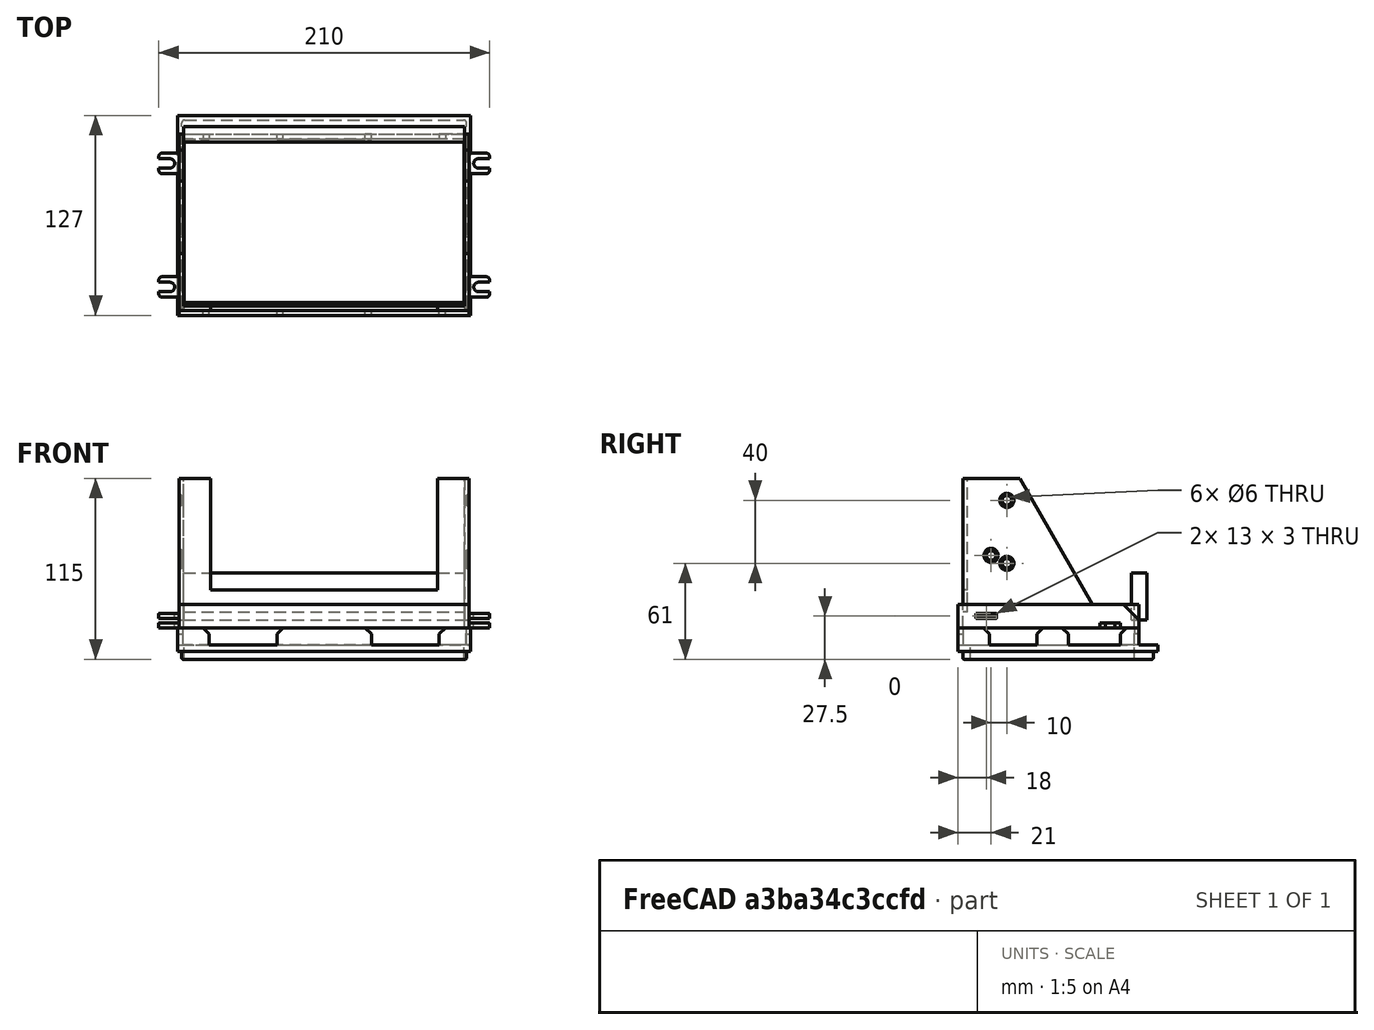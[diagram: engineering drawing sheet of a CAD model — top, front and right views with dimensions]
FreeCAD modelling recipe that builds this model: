
FCSTD DOCUMENT  (FreeCAD 0.15R4671 (Git))
Label: mount
License: All rights reserved
LicenseURL: http://en.wikipedia.org/wiki/All_rights_reserved
objects: Part::Box×30, Drawing::FeatureView×27, Part::Cut×14, Part::MultiFuse×13, Part::Cylinder×7, Drawing::FeatureViewPart×6, PartDesign::Fillet×4, Part::Fuse×2, Part::Fillet×2, Part::Chamfer×2, PartDesign::Chamfer×1, App::DocumentObjectGroup×1, Drawing::FeaturePage×1
note: 75 computed .brp shape members not serialized (recipe doc carries the construction recipe); baked Part::Feature solids carry a one-line shape summary decoded from their .brp

FEATURE [Part::Box] Box  label="Cube"
  Height = 15
  Length = 184
  Placement = pos=(1,0,5) rot=(0,0,1;0rad)
  Width = 115
FEATURE [Part::Box] Box001  label="Cube001"
  Height = 30
  Length = 178.5
  Placement = pos=(3.75,3,10) rot=(0,0,1;0rad)
  Width = 109
FEATURE [Part::Cylinder] Cylinder
  Angle = 360
  Height = 10
  Placement = pos=(7,6.5,0) rot=(0,0,1;0rad)
  Radius = 3
FEATURE [Part::Box] Box003  label="Cube003"
  Height = 10
  Length = 7
  Placement = pos=(0,3.5,0) rot=(0,0,1;0rad)
  Width = 6
FEATURE [PartDesign::Fillet] Fillet001
  Radius = 2
FEATURE [Part::MultiFuse] Fusion
  Shapes = -> [Box003,Cylinder]
FEATURE [Part::Cut] Cut001  label="Mounting Point 001"
  Base = -> Fillet001
  Placement = pos=(-12,11.5,11) rot=(0,0,1;0rad)
  Tool = -> Fusion
FEATURE [Part::Cylinder] Cylinder001
  Angle = 360
  Height = 10
  Placement = pos=(7,6.5,0) rot=(0,0,1;0rad)
  Radius = 3
FEATURE [Part::Box] Box005  label="Cube005"
  Height = 10
  Length = 7
  Placement = pos=(0,3.5,0) rot=(0,0,1;0rad)
  Width = 6
FEATURE [PartDesign::Fillet] Fillet003
  Radius = 2
FEATURE [Part::MultiFuse] Fusion001
  Shapes = -> [Box005,Cylinder001]
FEATURE [Part::Cut] Cut002  label="Mounting Point 002"
  Base = -> Fillet003
  Placement = pos=(-12,90,5) rot=(0,0,1;0rad)
  Tool = -> Fusion001
FEATURE [Part::Cylinder] Cylinder002
  Angle = 360
  Height = 10
  Placement = pos=(7,6.5,0) rot=(0,0,1;0rad)
  Radius = 3
FEATURE [Part::Box] Box007  label="Cube007"
  Height = 10
  Length = 7
  Placement = pos=(0,3.5,0) rot=(0,0,1;0rad)
  Width = 6
FEATURE [PartDesign::Fillet] Fillet005
  Radius = 2
FEATURE [Part::MultiFuse] Fusion002
  Shapes = -> [Box007,Cylinder002]
FEATURE [Part::Cut] Cut003  label="Mounting Point 003"
  Base = -> Fillet005
  Placement = pos=(198,24.5,11) rot=(0,0,1;3.14159rad)
  Tool = -> Fusion002
FEATURE [Part::Cylinder] Cylinder003
  Angle = 360
  Height = 10
  Placement = pos=(7,6.5,0) rot=(0,0,1;0rad)
  Radius = 3
FEATURE [Part::Box] Box009  label="Cube009"
  Height = 10
  Length = 7
  Placement = pos=(0,3.5,0) rot=(0,0,1;0rad)
  Width = 6
FEATURE [PartDesign::Fillet] Fillet007
  Radius = 2
FEATURE [Part::MultiFuse] Fusion003
  Shapes = -> [Box009,Cylinder003]
FEATURE [Part::Cut] Cut004  label="Mounting Point 004"
  Base = -> Fillet007
  Placement = pos=(198,103,5) rot=(0,0,1;3.14159rad)
  Tool = -> Fusion003
FEATURE [Part::Box] Box010  label="Cube010"
  Height = 80
  Length = 2.75
  Placement = pos=(0,10,30) rot=(0,0,1;0rad)
  Width = 80
FEATURE [Part::Box] Box011  label="Cube011"
  Height = 80
  Length = 4
  Placement = pos=(0,38,119) rot=(-1,0,0;1.0472rad)
  Width = 150
FEATURE [Part::Cut] Cut005
  Base = -> Box010
  Tool = -> Box011
FEATURE [Part::Box] Box012  label="Cube012"
  Height = 80
  Length = 20
  Placement = pos=(0,7,30) rot=(0,0,1;0rad)
  Width = 3
FEATURE [Part::Fuse] Fusion005  label="Left Support"
  Base = -> Cut005
  Placement = pos=(0,-3,0) rot=(0,0,1;0rad)
  Tool = -> Box012
FEATURE [Part::Box] Box013  label="Cube013"
  Height = 80
  Length = 2.75
  Placement = pos=(-2.75,10,30) rot=(0,0,1;0rad)
  Width = 80
FEATURE [Part::Box] Box014  label="Cube014"
  Height = 80
  Length = 4
  Placement = pos=(-2.75,38,119) rot=(-1,0,0;1.0472rad)
  Width = 150
FEATURE [Part::Cut] Cut006
  Base = -> Box013
  Tool = -> Box014
FEATURE [Part::Box] Box015  label="Cube015"
  Height = 80
  Length = 20
  Placement = pos=(-20,7,30) rot=(0,0,1;0rad)
  Width = 3
FEATURE [Part::Fuse] Fusion006  label="Right Support"
  Base = -> Cut006
  Placement = pos=(184,-3,0) rot=(0,0,1;0rad)
  Tool = -> Box015
FEATURE [Part::Box] Box016  label="Cross Brace"
  Height = 14
  Length = 184
  Placement = pos=(0,4,25) rot=(0,0,1;0rad)
  Width = 3
FEATURE [Part::Box] Box017  label="Lip"
  Height = 4
  Length = 186
  Width = 127
FEATURE [Part::Box] Box018  label="Cutout"
  Height = 30
  Length = 178
  Placement = pos=(4,8,-25) rot=(0,0,1;0rad)
  Width = 104
FEATURE [Part::Box] Box019  label="Cube016"
  Height = 5
  Length = 181
  Placement = pos=(2.5,3,-5) rot=(0,0,1;0rad)
  Width = 121
FEATURE [Part::MultiFuse] Fusion007
  Shapes = -> [Box017,Box019]
FEATURE [Part::Cut] Cut007
  Base = -> Fusion007
  Tool = -> Box018
FEATURE [Part::Fillet] Fillet008  label="Fill Plate"
  Base = -> Cut007
  Edges = 4 edges r=2: [Edge30,Edge31,Edge32,Edge35]
FEATURE [Part::MultiFuse] Fusion008  label="Carrier"
  Placement = pos=(1,-1,0) rot=(0,0,1;0rad)
  Shapes = -> [Fusion005,Fusion006,Box016]
FEATURE [Part::MultiFuse] Fusion009
  Placement = pos=(0,0,10) rot=(0,0,1;0rad)
  Shapes = -> [Box,Cut001,Cut002,Cut003,Cut004]
FEATURE [Part::Cut] Cut  label="Mount Points"
  Base = -> Fusion009
  Tool = -> Box001
FEATURE [Part::Box] Box020  label="Cube017"
  Height = 30
  Length = 178.5
  Placement = pos=(3.75,110,20) rot=(0,0,1;0rad)
  Width = 10
FEATURE [PartDesign::Chamfer] Chamfer  label="Carrier Frame"
  Size = 10
FEATURE [Part::Box] Box021  label="Cube018"
  Height = 11
  Length = 20
  Width = 20
FEATURE [Part::Box] Box022  label="Cube019"
  Height = 11
  Length = 30
  Placement = pos=(3,3,0) rot=(0,0,1;0rad)
  Width = 20
FEATURE [Part::Cut] Cut009
  Base = -> Box021
  Placement = pos=(0,0,4) rot=(0,0,1;0rad)
  Tool = -> Box022
FEATURE [Part::Box] Box023  label="Cube020"
  Height = 11
  Length = 20
  Width = 20
FEATURE [Part::Box] Box024  label="Cube021"
  Height = 11
  Length = 30
  Placement = pos=(3,3,0) rot=(0,0,1;0rad)
  Width = 20
FEATURE [Part::Cut] Cut010
  Base = -> Box023
  Placement = pos=(186,0,15) rot=(0,1,0;3.14159rad)
  Tool = -> Box024
FEATURE [Part::Box] Box025  label="Cube022"
  Height = 11
  Length = 3
  Placement = pos=(0,50,4) rot=(0,0,1;0rad)
  Width = 20
FEATURE [Part::Box] Box026  label="Cube023"
  Height = 11
  Length = 3
  Placement = pos=(183,50,4) rot=(0,0,1;0rad)
  Width = 20
FEATURE [Part::MultiFuse] Fusion012  label="Carrier (No Mounts)"
  Shapes = -> [Chamfer,Fusion008]
FEATURE [Drawing::FeatureViewPart] Ortho  label="Ortho_0_0"
  Direction = (0,0,-1)
  HiddenWidth = 0.15
  LineWidth = 0.35
  Rotation = 180
  ShowHiddenLines = false
  ShowSmoothLines = false
  Source = -> Fusion012
  Tolerance = 0.05
  ViewResult = <blob: 2978 chars omitted>
  Visible = true
  X = 60
  Y = 220
FEATURE [Drawing::FeatureView] dim007
  Rotation = 0
  ViewResult = <g> \n  <line x1="48.000000" y1="231.500000" x2="48.000000" y2="209.663479" style="stroke:rgb(0,0,0);stroke-width:0.30" />\n<line x1="61.000000" y1="218.000000" x2="61.000000" y2="209.663479" style="stroke:rgb(0,0,0);stroke-width:0.30" />\n<line x1="48.000000" y1="210.663479" x2="61.000000" y2="210.663479" style="stroke:rgb(0,0,0);stroke-width:0.30" /> \n  <polygon points="61.000000,210.663479 58.000000,209.663479 57.000000,210.663479 58.000000,211.663479" style="fill:rgb(0,0,0);stroke:rgb(0,0,0);stroke-width:0" /><polygon points="48.000000,210.663479 51.000000,211.663479 52.000000,210.663479 51.000000,209.663479" style="fill:rgb(0,0,0);stroke:rgb(0,0,0);stroke-width:0" /> \n  <text x="54.500000" y="208.663479" font-family="arial" font-size="3.6" fill="rgb(0,0,0)" text-anchor="middle" transform="rotate(0.000000 54.500000,208.663479)" >13</text> </g>
  Visible = true
  X = 0
  Y = 0
FEATURE [Drawing::FeatureView] dim008
  Rotation = 0
  ViewResult = <g> \n  <line x1="48.000000" y1="231.500000" x2="34.256570" y2="231.500000" style="stroke:rgb(0,0,0);stroke-width:0.30" />\n<line x1="48.000000" y1="244.500000" x2="34.256570" y2="244.500000" style="stroke:rgb(0,0,0);stroke-width:0.30" />\n<line x1="35.256570" y1="231.500000" x2="35.256570" y2="244.500000" style="stroke:rgb(0,0,0);stroke-width:0.30" /> \n  <polygon points="35.256570,244.500000 36.256570,241.500000 35.256570,240.500000 34.256570,241.500000" style="fill:rgb(0,0,0);stroke:rgb(0,0,0);stroke-width:0" /><polygon points="35.256570,231.500000 34.256570,234.500000 35.256570,235.500000 36.256570,234.500000" style="fill:rgb(0,0,0);stroke:rgb(0,0,0);stroke-width:0" /> \n  <text x="33.256570" y="238.000000" font-family="arial" font-size="3.6" fill="rgb(0,0,0)" text-anchor="middle" transform="rotate(-90.000000 33.256570,238.000000)" >13</text> </g>
  Visible = true
  X = 0
  Y = 0
FEATURE [Drawing::FeatureView] dim009
  Rotation = 0
  ViewResult = <g> \n  <line x1="63.750000" y1="228.000000" x2="63.750000" y2="300.005281" style="stroke:rgb(0,0,0);stroke-width:0.30" />\n<line x1="242.250000" y1="228.000000" x2="242.250000" y2="300.005281" style="stroke:rgb(0,0,0);stroke-width:0.30" />\n<line x1="63.750000" y1="299.005281" x2="242.250000" y2="299.005281" style="stroke:rgb(0,0,0);stroke-width:0.30" /> \n  <polygon points="242.250000,299.005281 239.250000,298.005281 238.250000,299.005281 239.250000,300.005281" style="fill:rgb(0,0,0);stroke:rgb(0,0,0);stroke-width:0" /><polygon points="63.750000,299.005281 66.750000,300.005281 67.750000,299.005281 66.750000,298.005281" style="fill:rgb(0,0,0);stroke:rgb(0,0,0);stroke-width:0" /> \n  <text x="153.000000" y="297.005281" font-family="arial" font-size="3.6" fill="rgb(0,0,0)" text-anchor="middle" transform="rotate(0.000000 153.000000,297.005281)" >178.5</text> </g>
  Visible = true
  X = 0
  Y = 0
FEATURE [Drawing::FeatureView] dimStack001
  Rotation = 0
  ViewResult = <g> <line x1="244.250001" y1="226.000000" x2="267.334281" y2="226.000000" style="stroke:rgb(0,0,0);stroke-width:0.30" />\n<line x1="244.250001" y1="332.000000" x2="267.334281" y2="332.000000" style="stroke:rgb(0,0,0);stroke-width:0.30" />\n<line x1="266.334281" y1="226.000000" x2="266.334281" y2="332.000000" style="stroke:rgb(0,0,0);stroke-width:0.30" />\n<polygon points="266.334281,226.000000 265.334281,229.000000 266.334281,230.000000 267.334281,229.000000" style="fill:rgb(0,0,0);stroke:rgb(0,0,0);stroke-width:0" />\n<polygon points="266.334281,332.000000 267.334281,329.000000 266.334281,328.000000 265.334281,329.000000" style="fill:rgb(0,0,0);stroke:rgb(0,0,0);stroke-width:0" />\n<text x="264.334281" y="279.000000" font-family="arial" font-size="3.6" fill="rgb(0,0,0)" text-anchor="middle" transform="rotate(-90.000000 264.334281,279.000000)" >106</text> </g> \n<g> <line x1="244.250001" y1="226.000000" x2="274.334281" y2="226.000000" style="stroke:rgb(0,0,0);stroke-width:0.30" />\n<line x1="244.250001" y1="223.000000" x2="274.334281" y2="223.000000" style="stroke:rgb(0,0,0);stroke-width:0.30" />\n<line x1="273.334281" y1="226.000000" x2="273.334281" y2="223.000000" style="stroke:rgb(0,0,0);stroke-width:0.30" />\n<polygon points="273.334281,226.000000 272.334281,229.000000 273.334281,230.000000 274.334281,229.000000" style="fill:rgb(0,0,0);stroke:rgb(0,0,0);stroke-width:0" />\n<polygon points="273.334281,223.000000 274.334281,220.000000 273.334281,219.000000 272.334281,220.000000" style="fill:rgb(0,0,0);stroke:rgb(0,0,0);stroke-width:0" />\n<text x="271.334281" y="224.500000" font-family="arial" font-size="3.6" fill="rgb(0,0,0)" text-anchor="middle" transform="rotate(-90.000000 271.334281,224.500000)" >3</text> </g> 
  Visible = true
  X = 0
  Y = 0
FEATURE [Drawing::FeatureView] dim010
  Rotation = 0
  ViewResult = <g> \n  <line x1="61.000000" y1="337.000000" x2="61.000000" y2="354.805423" style="stroke:rgb(0,0,0);stroke-width:0.30" />\n<line x1="245.000000" y1="337.000000" x2="245.000000" y2="354.805423" style="stroke:rgb(0,0,0);stroke-width:0.30" />\n<line x1="61.000000" y1="353.805423" x2="245.000000" y2="353.805423" style="stroke:rgb(0,0,0);stroke-width:0.30" /> \n  <polygon points="245.000000,353.805423 242.000000,352.805423 241.000000,353.805423 242.000000,354.805423" style="fill:rgb(0,0,0);stroke:rgb(0,0,0);stroke-width:0" /><polygon points="61.000000,353.805423 64.000000,354.805423 65.000000,353.805423 64.000000,352.805423" style="fill:rgb(0,0,0);stroke:rgb(0,0,0);stroke-width:0" /> \n  <text x="153.000000" y="351.805423" font-family="arial" font-size="3.6" fill="rgb(0,0,0)" text-anchor="middle" transform="rotate(0.000000 153.000000,351.805423)" >184</text> </g>
  Visible = true
  X = 0
  Y = 0
FEATURE [Drawing::FeatureView] dim011
  Rotation = 0
  ViewResult = <g> \n  <line x1="313.000000" y1="220.000000" x2="298.480968" y2="220.000000" style="stroke:rgb(0,0,0);stroke-width:0.30" />\n<line x1="313.000000" y1="335.000000" x2="298.480968" y2="335.000000" style="stroke:rgb(0,0,0);stroke-width:0.30" />\n<line x1="299.480968" y1="220.000000" x2="299.480968" y2="335.000000" style="stroke:rgb(0,0,0);stroke-width:0.30" /> \n  <polygon points="299.480968,335.000000 300.480968,332.000000 299.480968,331.000000 298.480968,332.000000" style="fill:rgb(0,0,0);stroke:rgb(0,0,0);stroke-width:0" /><polygon points="299.480968,220.000000 298.480968,223.000000 299.480968,224.000000 300.480968,223.000000" style="fill:rgb(0,0,0);stroke:rgb(0,0,0);stroke-width:0" /> \n  <text x="297.480968" y="277.500000" font-family="arial" font-size="3.6" fill="rgb(0,0,0)" text-anchor="middle" transform="rotate(-90.000000 297.480968,277.500000)" >115</text> </g>
  Visible = true
  X = 0
  Y = 0
FEATURE [Drawing::FeatureView] dim012
  Rotation = 0
  ViewResult = <g> \n  <line x1="330.000000" y1="221.000000" x2="330.000000" y2="208.868834" style="stroke:rgb(0,0,0);stroke-width:0.30" />\n<line x1="410.000000" y1="221.000000" x2="410.000000" y2="208.868834" style="stroke:rgb(0,0,0);stroke-width:0.30" />\n<line x1="330.000000" y1="209.868834" x2="410.000000" y2="209.868834" style="stroke:rgb(0,0,0);stroke-width:0.30" /> \n  <polygon points="410.000000,209.868834 407.000000,208.868834 406.000000,209.868834 407.000000,210.868834" style="fill:rgb(0,0,0);stroke:rgb(0,0,0);stroke-width:0" /><polygon points="330.000000,209.868834 333.000000,210.868834 334.000000,209.868834 333.000000,208.868834" style="fill:rgb(0,0,0);stroke:rgb(0,0,0);stroke-width:0" /> \n  <text x="370.000000" y="207.868834" font-family="arial" font-size="3.6" fill="rgb(0,0,0)" text-anchor="middle" transform="rotate(0.000000 370.000000,207.868834)" >80</text> </g>
  Visible = true
  X = 0
  Y = 0
FEATURE [Drawing::FeatureView] dim013
  Rotation = 0
  ViewResult = <g> \n  <line x1="321.000000" y1="229.512600" x2="321.000000" y2="200.380915" style="stroke:rgb(0,0,0);stroke-width:0.30" />\n<line x1="315.000000" y1="218.000000" x2="315.000000" y2="200.380915" style="stroke:rgb(0,0,0);stroke-width:0.30" />\n<line x1="321.000000" y1="201.380915" x2="315.000000" y2="201.380915" style="stroke:rgb(0,0,0);stroke-width:0.30" /> \n  <polygon points="315.000000,201.380915 312.000000,200.380915 311.000000,201.380915 312.000000,202.380915" style="fill:rgb(0,0,0);stroke:rgb(0,0,0);stroke-width:0" /><polygon points="321.000000,201.380915 324.000000,202.380915 325.000000,201.380915 324.000000,200.380915" style="fill:rgb(0,0,0);stroke:rgb(0,0,0);stroke-width:0" /> \n  <text x="318.000000" y="199.380915" font-family="arial" font-size="3.6" fill="rgb(0,0,0)" text-anchor="middle" transform="rotate(0.000000 318.000000,199.380915)" >6</text> </g>
  Visible = true
  X = 0
  Y = 0
FEATURE [Drawing::FeatureView] dim014
  Rotation = 0
  ViewResult = <g> \n  <line x1="315.000000" y1="337.000000" x2="315.000000" y2="355.145058" style="stroke:rgb(0,0,0);stroke-width:0.30" />\n<line x1="330.000000" y1="327.000000" x2="330.000000" y2="355.145058" style="stroke:rgb(0,0,0);stroke-width:0.30" />\n<line x1="315.000000" y1="354.145058" x2="330.000000" y2="354.145058" style="stroke:rgb(0,0,0);stroke-width:0.30" /> \n  <polygon points="330.000000,354.145058 327.000000,353.145058 326.000000,354.145058 327.000000,355.145058" style="fill:rgb(0,0,0);stroke:rgb(0,0,0);stroke-width:0" /><polygon points="315.000000,354.145058 318.000000,355.145058 319.000000,354.145058 318.000000,353.145058" style="fill:rgb(0,0,0);stroke:rgb(0,0,0);stroke-width:0" /> \n  <text x="322.500000" y="352.145058" font-family="arial" font-size="3.6" fill="rgb(0,0,0)" text-anchor="middle" transform="rotate(0.000000 322.500000,352.145058)" >15</text> </g>
  Visible = true
  X = 0
  Y = 0
FEATURE [Part::Cylinder] Cylinder004
  Angle = 360
  Height = 200
  Placement = pos=(0,0,0) rot=(0,1,0;1.5708rad)
  Radius = 3
FEATURE [Part::Cylinder] Cylinder005
  Angle = 360
  Height = 200
  Placement = pos=(0,0,40) rot=(0,1,0;1.5708rad)
  Radius = 3
FEATURE [Part::Cylinder] Cylinder006
  Angle = 360
  Height = 200
  Placement = pos=(0,-10,5) rot=(0,1,0;1.5708rad)
  Radius = 3
FEATURE [Part::MultiFuse] Fusion013
  Placement = pos=(-5,31,56) rot=(0,0,1;0rad)
  Shapes = -> [Cylinder004,Cylinder005,Cylinder006]
FEATURE [Part::Cut] Cut011
  Base = -> Fusion012
  Tool = -> Fusion013
FEATURE [Part::Chamfer] Chamfer005  label="Carrier (Complete)"
  Base = -> Cut011
  Edges = 6 edges r=1.5: [Edge86,Edge87,Edge88,Edge199,Edge200,Edge201]
FEATURE [Drawing::FeatureViewPart] Ortho008  label="Ortho_0_003"
  Direction = (1,0,0)
  HiddenWidth = 0.15
  LineWidth = 0.35
  Rotation = 0
  ShowHiddenLines = false
  ShowSmoothLines = false
  Source = -> Chamfer005
  Tolerance = 0.05
  ViewResult = <blob: 5883 chars omitted>
  Visible = true
  X = 300
  Y = 220
FEATURE [Drawing::FeatureViewPart] Ortho010  label="Ortho_1_002"
  Direction = (0.57735,-0.57735,-0.57735)
  HiddenWidth = 0.15
  LineWidth = 0.35
  Rotation = 180
  ShowHiddenLines = false
  ShowSmoothLines = false
  Source = -> Chamfer005
  Tolerance = 0.05
  ViewResult = <blob: 11598 chars omitted>
  Visible = true
  X = 360
  Y = 60
FEATURE [Part::Box] Box029  label="Cube026"
  Height = 11
  Length = 20
  Width = 20
FEATURE [Part::Box] Box030  label="Cube027"
  Height = 11
  Length = 30
  Placement = pos=(3,3,0) rot=(0,0,1;0rad)
  Width = 20
FEATURE [Part::Cut] Cut012
  Base = -> Box029
  Placement = pos=(0,115,15) rot=(1,0,0;3.14159rad)
  Tool = -> Box030
FEATURE [Part::Box] Box031  label="Cube028"
  Height = 11
  Length = 20
  Width = 20
FEATURE [Part::Box] Box032  label="Cube029"
  Height = 11
  Length = 30
  Placement = pos=(3,3,0) rot=(0,0,1;0rad)
  Width = 20
FEATURE [Part::Cut] Cut013
  Base = -> Box031
  Placement = pos=(186,115,4) rot=(0,0,1;3.14159rad)
  Tool = -> Box032
FEATURE [Part::MultiFuse] Fusion014
  Shapes = -> [Cut009,Box025,Box026,Cut010,Cut013,Cut012]
FEATURE [Part::Box] Box033  label="Cube030"
  Height = 11
  Length = 60
  Placement = pos=(63,112,4) rot=(0,0,1;0rad)
  Width = 3
FEATURE [Part::MultiFuse] Fusion015
  Shapes = -> [Fusion014,Box033]
FEATURE [Part::Fillet] Fillet009
  Base = -> Fillet008
  Edges = 8 edges r=1: [Edge13,Edge16,Edge18,Edge21,Edge23,Edge24,Edge26,Edge28]
FEATURE [Part::Box] Box034  label="Cube031"
  Height = 20
  Length = 200
  Placement = pos=(-10,73,-5) rot=(0,0,1;0rad)
  Width = 30
FEATURE [Part::Cut] Cut014
  Base = -> Fusion015
  Tool = -> Box034
FEATURE [Part::Box] Box035  label="Cube032"
  Height = 11
  Length = 60
  Placement = pos=(63,0,4) rot=(0,0,1;0rad)
  Width = 3
FEATURE [Part::MultiFuse] Fusion016
  Shapes = -> [Cut014,Box035]
FEATURE [Part::Chamfer] Chamfer006
  Base = -> Fusion016
  Edges = 16 edges r=4: [Edge12,Edge16,Edge20,Edge24,Edge41,Edge44,Edge58,Edge60,Edge65,Edge68,Edge80,Edge84,Edge100,Edge102,Edge110,Edge113]
FEATURE [Part::MultiFuse] Fusion017  label="Fascia (Complete)"
  Shapes = -> [Fillet009,Chamfer006]
FEATURE [Drawing::FeatureViewPart] Ortho011  label="Ortho_0_004"
  Direction = (0,0,-1)
  HiddenWidth = 0.15
  LineWidth = 0.35
  Rotation = 180
  ShowHiddenLines = false
  ShowSmoothLines = false
  Source = -> Fusion017
  Tolerance = 0.05
  ViewResult = <g id="Ortho_0_004"\n   transform="rotate(180,60,50) translate(60,50) scale(1,1)"\n  >\n<g   stroke="rgb(0, 0, 0)"\n   stroke-width="0.35"\n   stroke-linecap="butt"\n   stroke-linejoin="miter"\n   fill="none"\n   transform="scale(1,-1)"\n  >\n<path id= "1" d=" M -4.5 124 L -181.5 124 " />\n<path id= "2" d=" M 0 0 L 0 127 " />\n<path id= "3" d=" M 0 127 L -186 127 " />\n<path id= "4" d=" M 0 0 L -186 0 " />\n<path id= "5" d=" M -186 0 L -186 127 " />\n<path d="M-2.5 122 A2 2 0 0 1 -4.5 124" /><path id= "7" d=" M -2.5 5 L -2.5 122 " />\n<path id= "8" d=" M -182 8 L -182 112 " />\n<path id= "9" d=" M -182 112 L -4 112 " />\n<path id= "10" d=" M -4 8 L -4 112 " />\n<path id= "11" d=" M -182 8 L -4 8 " />\n<path d="M-181.5 124 A2 2 0 0 1 -183.5 122" /><path id= "13" d=" M -183.5 122 L -183.5 5 " />\n<path id= "14" d=" M -181.5 3 L -4.5 3 " />\n<path d="M-4.5 3 A2 2 0 0 1 -2.5 5" /><path d="M-183.5 5 A2 2 0 0 1 -181.5 3" /></g>\n</g>
  Visible = true
  X = 60
  Y = 50
FEATURE [Drawing::FeatureViewPart] Ortho013  label="Ortho_1_1"
  Direction = (0.57735,-0.57735,-0.57735)
  HiddenWidth = 0.15
  LineWidth = 0.35
  Rotation = 180
  ShowHiddenLines = false
  ShowSmoothLines = false
  Source = -> Fusion017
  Tolerance = 0.05
  ViewResult = <blob: 7080 chars omitted>
  Visible = true
  X = 360
  Y = 60
FEATURE [Drawing::FeatureViewPart] Ortho014  label="Ortho_0_005"
  Direction = (1,0,0)
  HiddenWidth = 0.15
  LineWidth = 0.35
  Rotation = 0
  ShowHiddenLines = false
  ShowSmoothLines = false
  Source = -> Fusion017
  Tolerance = 0.05
  ViewResult = <blob: 2171 chars omitted>
  Visible = true
  X = 295
  Y = 50
FEATURE [App::DocumentObjectGroup] Group  label="Components"
  Group = -> [Cut,Box020]
FEATURE [Drawing::FeatureView] dim001
  Rotation = 0
  ViewResult = <g   >\n<line x1="66.000000" y1="58.000000" x2="108.161899" y2="58.000000" style="stroke:rgb(0,0,0);stroke-width:0.30" />\n<line x1="66.000000" y1="162.000000" x2="108.161899" y2="162.000000" style="stroke:rgb(0,0,0);stroke-width:0.30" />\n<line x1="107.161899" y1="58.000000" x2="107.161899" y2="162.000000" style="stroke:rgb(0,0,0);stroke-width:0.30" />\n<polygon points="107.161899,58.000000 106.161899,61.000000 107.161899,62.000000 108.161899,61.000000" style="fill:rgb(0,0,0);stroke:rgb(0,0,0);stroke-width:0" /><polygon points="107.161899,162.000000 108.161899,159.000000 107.161899,158.000000 106.161899,159.000000" style="fill:rgb(0,0,0);stroke:rgb(0,0,0);stroke-width:0" />\n<text x="104.623854" y="112.237988" font-family="Arial" font-size="3.6" fill="rgb(0,0,0)" text-anchor="inherit" transform="rotate(-90.000000 104.623854,112.237988)" >104</text>\n</g> 
  Visible = true
  X = 0
  Y = 0
FEATURE [Drawing::FeatureView] dim002
  Rotation = 0
  ViewResult = <g   >\n<line x1="242.000000" y1="60.000000" x2="242.000000" y2="120.852123" style="stroke:rgb(0,0,0);stroke-width:0.30" />\n<line x1="64.000000" y1="60.000000" x2="64.000000" y2="120.852123" style="stroke:rgb(0,0,0);stroke-width:0.30" />\n<line x1="242.000000" y1="119.852123" x2="64.000000" y2="119.852123" style="stroke:rgb(0,0,0);stroke-width:0.30" />\n<polygon points="242.000000,119.852123 239.000000,118.852123 238.000000,119.852123 239.000000,120.852123" style="fill:rgb(0,0,0);stroke:rgb(0,0,0);stroke-width:0" /><polygon points="64.000000,119.852123 67.000000,120.852123 68.000000,119.852123 67.000000,118.852123" style="fill:rgb(0,0,0);stroke:rgb(0,0,0);stroke-width:0" />\n<text x="119.570118" y="117.596083" font-family="Arial" font-size="3.6" fill="rgb(0,0,0)" text-anchor="inherit" transform="rotate(0.000000 119.570118,117.596083)" >178</text>\n</g> 
  Visible = true
  X = 0
  Y = 0
FEATURE [Drawing::FeatureView] dim003
  Rotation = 0
  ViewResult = <g   >\n<line x1="295.000000" y1="48.000000" x2="295.000000" y2="38.198694" style="stroke:rgb(0,0,0);stroke-width:0.30" />\n<line x1="310.000000" y1="48.000000" x2="310.000000" y2="38.198694" style="stroke:rgb(0,0,0);stroke-width:0.30" />\n<line x1="295.000000" y1="39.198694" x2="310.000000" y2="39.198694" style="stroke:rgb(0,0,0);stroke-width:0.30" />\n<polygon points="295.000000,39.198694 298.000000,40.198694 299.000000,39.198694 298.000000,38.198694" style="fill:rgb(0,0,0);stroke:rgb(0,0,0);stroke-width:0" /><polygon points="310.000000,39.198694 307.000000,38.198694 306.000000,39.198694 307.000000,40.198694" style="fill:rgb(0,0,0);stroke:rgb(0,0,0);stroke-width:0" />\n<text x="300.053316" y="36.942654" font-family="Arial" font-size="3.6" fill="rgb(0,0,0)" text-anchor="inherit" transform="rotate(0.000000 300.053316,36.942654)" >15</text>\n</g> 
  Visible = true
  X = 0
  Y = 0
FEATURE [Drawing::FeatureView] dim004
  Rotation = 0
  ViewResult = <g   >\n<line x1="295.000000" y1="179.000000" x2="295.000000" y2="188.815327" style="stroke:rgb(0,0,0);stroke-width:0.30" />\n<line x1="299.000000" y1="179.000000" x2="299.000000" y2="188.815327" style="stroke:rgb(0,0,0);stroke-width:0.30" />\n<line x1="295.000000" y1="187.815327" x2="299.000000" y2="187.815327" style="stroke:rgb(0,0,0);stroke-width:0.30" />\n<polygon points="295.000000,187.815327 292.000000,186.815327 291.000000,187.815327 292.000000,188.815327" style="fill:rgb(0,0,0);stroke:rgb(0,0,0);stroke-width:0" /><polygon points="299.000000,187.815327 302.000000,188.815327 303.000000,187.815327 302.000000,186.815327" style="fill:rgb(0,0,0);stroke:rgb(0,0,0);stroke-width:0" />\n<text x="296.669256" y="193.455427" font-family="Arial" font-size="3.6" fill="rgb(0,0,0)" text-anchor="inherit" transform="rotate(0.000000 296.669256,193.455427)" >4</text>\n</g> 
  Visible = true
  X = 0
  Y = 0
FEATURE [Drawing::FeatureView] dim005
  Rotation = 0
  ViewResult = <g   >\n<line x1="293.000000" y1="177.000000" x2="281.851011" y2="177.000000" style="stroke:rgb(0,0,0);stroke-width:0.30" />\n<line x1="289.000000" y1="174.000000" x2="281.851011" y2="174.000000" style="stroke:rgb(0,0,0);stroke-width:0.30" />\n<line x1="282.851011" y1="177.000000" x2="282.851011" y2="174.000000" style="stroke:rgb(0,0,0);stroke-width:0.30" />\n<polygon points="282.851011,177.000000 281.851011,180.000000 282.851011,181.000000 283.851011,180.000000" style="fill:rgb(0,0,0);stroke:rgb(0,0,0);stroke-width:0" /><polygon points="282.851011,174.000000 283.851011,171.000000 282.851011,170.000000 281.851011,171.000000" style="fill:rgb(0,0,0);stroke:rgb(0,0,0);stroke-width:0" />\n<text x="278.338931" y="176.535128" font-family="Arial" font-size="3.6" fill="rgb(0,0,0)" text-anchor="inherit" transform="rotate(-90.000000 278.338931,176.535128)" >3</text>\n</g> 
  Visible = true
  X = 0
  Y = 0
FEATURE [Drawing::FeatureView] dim006
  Rotation = 0
  ViewResult = <g   >\n<line x1="243.500000" y1="53.000000" x2="257.342541" y2="53.000000" style="stroke:rgb(0,0,0);stroke-width:0.30" />\n<line x1="243.500000" y1="174.000000" x2="257.342541" y2="174.000000" style="stroke:rgb(0,0,0);stroke-width:0.30" />\n<line x1="256.342541" y1="53.000000" x2="256.342541" y2="174.000000" style="stroke:rgb(0,0,0);stroke-width:0.30" />\n<polygon points="256.342541,53.000000 255.342541,56.000000 256.342541,57.000000 257.342541,56.000000" style="fill:rgb(0,0,0);stroke:rgb(0,0,0);stroke-width:0" /><polygon points="256.342541,174.000000 257.342541,171.000000 256.342541,170.000000 255.342541,171.000000" style="fill:rgb(0,0,0);stroke:rgb(0,0,0);stroke-width:0" />\n<text x="261.700636" y="115.904053" font-family="Arial" font-size="3.6" fill="rgb(0,0,0)" text-anchor="inherit" transform="rotate(-90.000000 261.700636,115.904053)" >121</text>\n</g> 
  Visible = true
  X = 0
  Y = 0
FEATURE [Drawing::FeatureView] dim015
  Rotation = 0
  ViewResult = <g   >\n<line x1="62.500000" y1="174.000000" x2="62.500000" y2="188.815327" style="stroke:rgb(0,0,0);stroke-width:0.30" />\n<line x1="243.500000" y1="174.000000" x2="243.500000" y2="188.815327" style="stroke:rgb(0,0,0);stroke-width:0.30" />\n<line x1="62.500000" y1="187.815327" x2="243.500000" y2="187.815327" style="stroke:rgb(0,0,0);stroke-width:0.30" />\n<polygon points="62.500000,187.815327 65.500000,188.815327 66.500000,187.815327 65.500000,186.815327" style="fill:rgb(0,0,0);stroke:rgb(0,0,0);stroke-width:0" /><polygon points="243.500000,187.815327 240.500000,186.815327 239.500000,187.815327 240.500000,188.815327" style="fill:rgb(0,0,0);stroke:rgb(0,0,0);stroke-width:0" />\n<text x="150.590668" y="193.455427" font-family="Arial" font-size="3.6" fill="rgb(0,0,0)" text-anchor="inherit" transform="rotate(0.000000 150.590668,193.455427)" >181</text>\n</g> 
  Visible = true
  X = 0
  Y = 0
FEATURE [Drawing::FeatureView] dim016
  Rotation = 0
  ViewResult = <g   >\n<line x1="58.000000" y1="177.000000" x2="46.376839" y2="177.000000" style="stroke:rgb(0,0,0);stroke-width:0.30" />\n<line x1="58.000000" y1="50.000000" x2="46.376839" y2="50.000000" style="stroke:rgb(0,0,0);stroke-width:0.30" />\n<line x1="47.376839" y1="177.000000" x2="47.376839" y2="50.000000" style="stroke:rgb(0,0,0);stroke-width:0.30" />\n<polygon points="47.376839,177.000000 48.376839,174.000000 47.376839,173.000000 46.376839,174.000000" style="fill:rgb(0,0,0);stroke:rgb(0,0,0);stroke-width:0" /><polygon points="47.376839,50.000000 46.376839,53.000000 47.376839,54.000000 48.376839,53.000000" style="fill:rgb(0,0,0);stroke:rgb(0,0,0);stroke-width:0" />\n<text x="44.274784" y="117.314078" font-family="Arial" font-size="3.6" fill="rgb(0,0,0)" text-anchor="inherit" transform="rotate(-90.000000 44.274784,117.314078)" >127</text>\n</g> 
  Visible = true
  X = 0
  Y = 0
FEATURE [Drawing::FeatureView] dim017
  Rotation = 0
  ViewResult = <g   >\n<line x1="60.000000" y1="48.000000" x2="60.000000" y2="37.070674" style="stroke:rgb(0,0,0);stroke-width:0.30" />\n<line x1="246.000000" y1="48.000000" x2="246.000000" y2="37.070674" style="stroke:rgb(0,0,0);stroke-width:0.30" />\n<line x1="60.000000" y1="38.070674" x2="246.000000" y2="38.070674" style="stroke:rgb(0,0,0);stroke-width:0.30" />\n<polygon points="60.000000,38.070674 63.000000,39.070674 64.000000,38.070674 63.000000,37.070674" style="fill:rgb(0,0,0);stroke:rgb(0,0,0);stroke-width:0" /><polygon points="246.000000,38.070674 243.000000,37.070674 242.000000,38.070674 243.000000,39.070674" style="fill:rgb(0,0,0);stroke:rgb(0,0,0);stroke-width:0" />\n<text x="149.462648" y="34.686615" font-family="Arial" font-size="3.6" fill="rgb(0,0,0)" text-anchor="inherit" transform="rotate(0.000000 149.462648,34.686615)" >186</text>\n</g> 
  Visible = true
  X = 0
  Y = 0
FEATURE [Drawing::FeatureView] centerLines001
  Rotation = 0
  ViewResult = <g  transform="scale(1.000000,1.000000)" stroke="rgb(0,0,0)"  stroke-width="0.300000" >\n<path d="M 356.000000,251.000000 L 356.000000,253.000000 "/>\n<path d="M 356.000000,251.000000 L 358.000000,251.000000 "/>\n<path d="M 356.000000,251.000000 L 356.000000,249.000000 "/>\n<path d="M 356.000000,251.000000 L 354.000000,251.000000 "/>\n</g> 
  Visible = true
  X = 0
  Y = 0
FEATURE [Drawing::FeatureView] centerLines002
  Rotation = 0
  ViewResult = <g  transform="scale(1.000000,1.000000)" stroke="rgb(0,0,0)"  stroke-width="0.300000" >\n<path d="M 361.000000,241.000000 L 361.000000,239.000000 "/>\n<path d="M 361.000000,241.000000 L 359.000000,241.000000 "/>\n<path d="M 361.000000,241.000000 L 361.000000,243.000000 "/>\n<path d="M 361.000000,241.000000 L 363.000000,241.000000 "/>\n</g> 
  Visible = true
  X = 0
  Y = 0
FEATURE [Drawing::FeatureView] centerLines003
  Rotation = 0
  ViewResult = <g  transform="scale(1.000000,1.000000)" stroke="rgb(0,0,0)"  stroke-width="0.300000" >\n<path d="M 396.000000,251.000000 L 396.000000,249.000000 "/>\n<path d="M 396.000000,251.000000 L 394.000000,251.000000 "/>\n<path d="M 396.000000,251.000000 L 396.000000,253.000000 "/>\n<path d="M 396.000000,251.000000 L 398.000000,251.000000 "/>\n</g> 
  Visible = true
  X = 0
  Y = 0
FEATURE [Drawing::FeatureView] dim018
  Rotation = 0
  ViewResult = <g   >\n<line x1="356.000000" y1="253.000000" x2="356.000000" y2="302.779073" style="stroke:rgb(0,0,0);stroke-width:0.30" />\n<line x1="396.000000" y1="253.000000" x2="396.000000" y2="302.779073" style="stroke:rgb(0,0,0);stroke-width:0.30" />\n<line x1="356.000000" y1="301.779073" x2="396.000000" y2="301.779073" style="stroke:rgb(0,0,0);stroke-width:0.30" />\n<polygon points="356.000000,301.779073 359.000000,302.779073 360.000000,301.779073 359.000000,300.779073" style="fill:rgb(0,0,0);stroke:rgb(0,0,0);stroke-width:0" /><polygon points="396.000000,301.779073 393.000000,300.779073 392.000000,301.779073 393.000000,302.779073" style="fill:rgb(0,0,0);stroke:rgb(0,0,0);stroke-width:0" />\n<text x="374.401888" y="306.538996" font-family="Arial" font-size="3.6" fill="rgb(0,0,0)" text-anchor="inherit" transform="rotate(0.000000 374.401888,306.538996)" >40</text>\n</g> 
  Visible = true
  X = 0
  Y = 0
FEATURE [Drawing::FeatureView] dim019
  Rotation = 0
  ViewResult = <g   >\n<line x1="363.000000" y1="241.000000" x2="423.409104" y2="241.000000" style="stroke:rgb(0,0,0);stroke-width:0.30" />\n<line x1="398.000000" y1="251.000000" x2="423.409104" y2="251.000000" style="stroke:rgb(0,0,0);stroke-width:0.30" />\n<line x1="422.409104" y1="241.000000" x2="422.409104" y2="251.000000" style="stroke:rgb(0,0,0);stroke-width:0.30" />\n<polygon points="422.409104,241.000000 423.409104,238.000000 422.409104,237.000000 421.409104,238.000000" style="fill:rgb(0,0,0);stroke:rgb(0,0,0);stroke-width:0" /><polygon points="422.409104,251.000000 421.409104,254.000000 422.409104,255.000000 423.409104,254.000000" style="fill:rgb(0,0,0);stroke:rgb(0,0,0);stroke-width:0" />\n<text x="427.849015" y="248.195948" font-family="Arial" font-size="3.6" fill="rgb(0,0,0)" text-anchor="inherit" transform="rotate(-90.000000 427.849015,248.195948)" >10</text>\n</g> 
  Visible = true
  X = 0
  Y = 0
FEATURE [Drawing::FeatureView] dim020
  Rotation = 0
  ViewResult = <g   >\n<line x1="356.000000" y1="249.000000" x2="356.000000" y2="219.316403" style="stroke:rgb(0,0,0);stroke-width:0.30" />\n<line x1="361.000000" y1="239.000000" x2="361.000000" y2="219.316403" style="stroke:rgb(0,0,0);stroke-width:0.30" />\n<line x1="356.000000" y1="220.316403" x2="361.000000" y2="220.316403" style="stroke:rgb(0,0,0);stroke-width:0.30" />\n<polygon points="356.000000,220.316403 353.000000,219.316403 352.000000,220.316403 353.000000,221.316403" style="fill:rgb(0,0,0);stroke:rgb(0,0,0);stroke-width:0" /><polygon points="361.000000,220.316403 364.000000,221.316403 365.000000,220.316403 364.000000,219.316403" style="fill:rgb(0,0,0);stroke:rgb(0,0,0);stroke-width:0" />\n<text x="357.402165" y="217.596448" font-family="Arial" font-size="3.6" fill="rgb(0,0,0)" text-anchor="inherit" transform="rotate(0.000000 357.402165,217.596448)" >5</text>\n</g> 
  Visible = true
  X = 0
  Y = 0
FEATURE [Drawing::FeatureView] dim021
  Rotation = 0
  ViewResult = <g   >\n<line x1="356.000000" y1="253.000000" x2="356.000000" y2="262.397166" style="stroke:rgb(0,0,0);stroke-width:0.30" />\n<line x1="330.000000" y1="228.000000" x2="330.000000" y2="262.397166" style="stroke:rgb(0,0,0);stroke-width:0.30" />\n<line x1="356.000000" y1="261.397166" x2="330.000000" y2="261.397166" style="stroke:rgb(0,0,0);stroke-width:0.30" />\n<polygon points="356.000000,261.397166 353.000000,260.397166 352.000000,261.397166 353.000000,262.397166" style="fill:rgb(0,0,0);stroke:rgb(0,0,0);stroke-width:0" /><polygon points="330.000000,261.397166 333.000000,262.397166 334.000000,261.397166 333.000000,260.397166" style="fill:rgb(0,0,0);stroke:rgb(0,0,0);stroke-width:0" />\n<text x="340.932094" y="259.013026" font-family="Arial" font-size="3.6" fill="rgb(0,0,0)" text-anchor="inherit" transform="rotate(0.000000 340.932094,259.013026)" >26</text>\n</g> 
  Visible = true
  X = 0
  Y = 0
FEATURE [Drawing::FeatureView] dim022
  Rotation = 0
  ViewResult = <g   >\n<line x1="254.000000" y1="244.500000" x2="254.496526" y2="244.500000" style="stroke:rgb(0,0,0);stroke-width:0.30" />\n<line x1="254.000000" y1="310.000000" x2="254.496526" y2="310.000000" style="stroke:rgb(0,0,0);stroke-width:0.30" />\n<line x1="255.496526" y1="244.500000" x2="255.496526" y2="310.000000" style="stroke:rgb(0,0,0);stroke-width:0.30" />\n<polygon points="255.496526,244.500000 254.496526,247.500000 255.496526,248.500000 256.496526,247.500000" style="fill:rgb(0,0,0);stroke:rgb(0,0,0);stroke-width:0" /><polygon points="255.496526,310.000000 256.496526,307.000000 255.496526,306.000000 254.496526,307.000000" style="fill:rgb(0,0,0);stroke:rgb(0,0,0);stroke-width:0" />\n<text x="253.240486" y="282.287001" font-family="Arial" font-size="3.6" fill="rgb(0,0,0)" text-anchor="inherit" transform="rotate(-90.000000 253.240486,282.287001)" >65.5</text>\n</g> 
  Visible = true
  X = 0
  Y = 0
FEATURE [Drawing::FeatureView] dim023
  Rotation = 0
  ViewResult = <g   >\n <line x1="410.000000" y1="261.196200" x2="410.000000" y2="336.163780" style="stroke:rgb(0,0,0);stroke-width:0.300000" />\n<path d = "M 344.210138 297.179977 A 75.967580 75.967580 0 0 0 410.000000 335.163780" style="stroke:rgb(0,0,0);stroke-width:0.30;fill:none" />\n<polygon points="344.210138,297.179977 344.844112,300.278053 346.210138,300.644079 346.576163,299.278053" style="fill:rgb(0,0,0);stroke:rgb(0,0,0);stroke-width:0" />\n<polygon points="410.000000,335.163780 407.000000,334.163780 406.000000,335.163780 407.000000,336.163780" style="fill:rgb(0,0,0);stroke:rgb(0,0,0);stroke-width:0" />\n<text x="412.965587" y="301.754028" font-family="Arial" font-size="3.6" fill="rgb(0,0,0)" text-anchor="1.50122509799"  >60.0°</text>\n <!--60.0000115676-->\n <!--%3.1f°-->\n</g> 
  Visible = true
  X = 0
  Y = 0
FEATURE [Drawing::FeaturePage] Page  label="Carrier Draft"
  EditableTexts = FLOYD DIEBEL | MIATA NA HU MOUNT | CARRIER AND FASCIA FOR |  JOYING JY-UL128n2  | A2 | X / Y | 1:1 | 1/2 | 2016-12-27 | A
  Group = -> [Ortho,dim007,dim008,dim009,dimStack001,dim010,dim011,dim012,dim013,dim014,Ortho008,Ortho010,Ortho011,Ortho013,Ortho014,dim001,dim002,dim003,dim004,dim005,dim006,dim015,dim016,dim017,centerLines001,centerLines002,centerLines003,dim018,dim019,dim020,dim021,dim022,dim023]
  Template = D:/Program Files/FreeCAD 0.15/data/Mod/Drawing/Templates/A2_Landscape_ISO7200.svg
